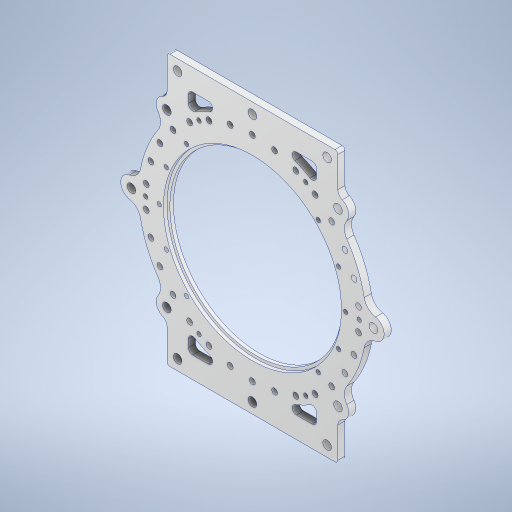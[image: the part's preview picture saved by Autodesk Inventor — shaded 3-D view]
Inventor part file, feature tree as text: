
AUTODESK INVENTOR PART (.ipt)
format: ipt  version: 2024 (Build 280153000, 153)  size: 693,248 bytes
history: native  units: mm
features: thread x11, sketch x11, extrude x6, hole x5, pattern_circular x3, fillet x2, projected_geometry x2, other x1
ambient origin geometry x8: Origin, YZ Plane, XZ Plane, XY Plane, X Axis, Y Axis, Z Axis, Center Point
bodies: Body1 (feature_tree)
feature tree (41):
  other  "ソリッド1"
  extrude  "押し出し1"  Depth=160.0mm
  extrude  "押し出し2"  Depth=5.0mm TaperAngle=0.0deg
  hole  "穴1"  [1 undecoded]
  pattern_circular  "円形状パターン1"  [2 undecoded]
  extrude  "押し出し3"  Depth=75.0mm
  hole  "穴2"  [1 undecoded]
  thread  "ねじ1"
  thread  "ねじ2"
  thread  "ねじ3"
  thread  "ねじ4"
  thread  "ねじ5"
  thread  "ねじ6"
  thread  "ねじ7"
  thread  "ねじ8"
  thread  "ねじ9"
  thread  "ねじ10"
  hole  "穴3"  [1 undecoded]
  thread  "ねじ11"
  pattern_circular  "円形状パターン2"  [2 undecoded]
  extrude  "押し出し4"  Depth=2.5mm TaperAngle=0.0deg
  hole  "穴4"  [1 undecoded]
  pattern_circular  "円形状パターン3"  [2 undecoded]
  extrude  "押し出し5"  Depth=160.0mm TaperAngle=360.0deg
  hole  "穴5"  [1 undecoded]
  fillet  "フィレット1"  Radius=5.0mm
  fillet  "フィレット2"  Radius=5.0mm
  extrude  "押し出し6"  Depth=5.0mm TaperAngle=0.0deg
  sketch  "スケッチ1"
  sketch  "スケッチ2"
  sketch  "スケッチ3"
  sketch  "スケッチ4"
  sketch  "スケッチ5"
  sketch  "スケッチ6"
  sketch  "スケッチ7"
  sketch  "スケッチ8"
  sketch  "スケッチ9"
  projected_geometry  "投影ループ1"
  sketch  "スケッチ10"
  sketch  "スケッチ11"
  projected_geometry  "投影ループ2"
note: 11 required parameter values undecoded (feature->parameter linkage not recoverable at this tier; creation-order binding heuristic only, values carry confidence <= 0.55)
